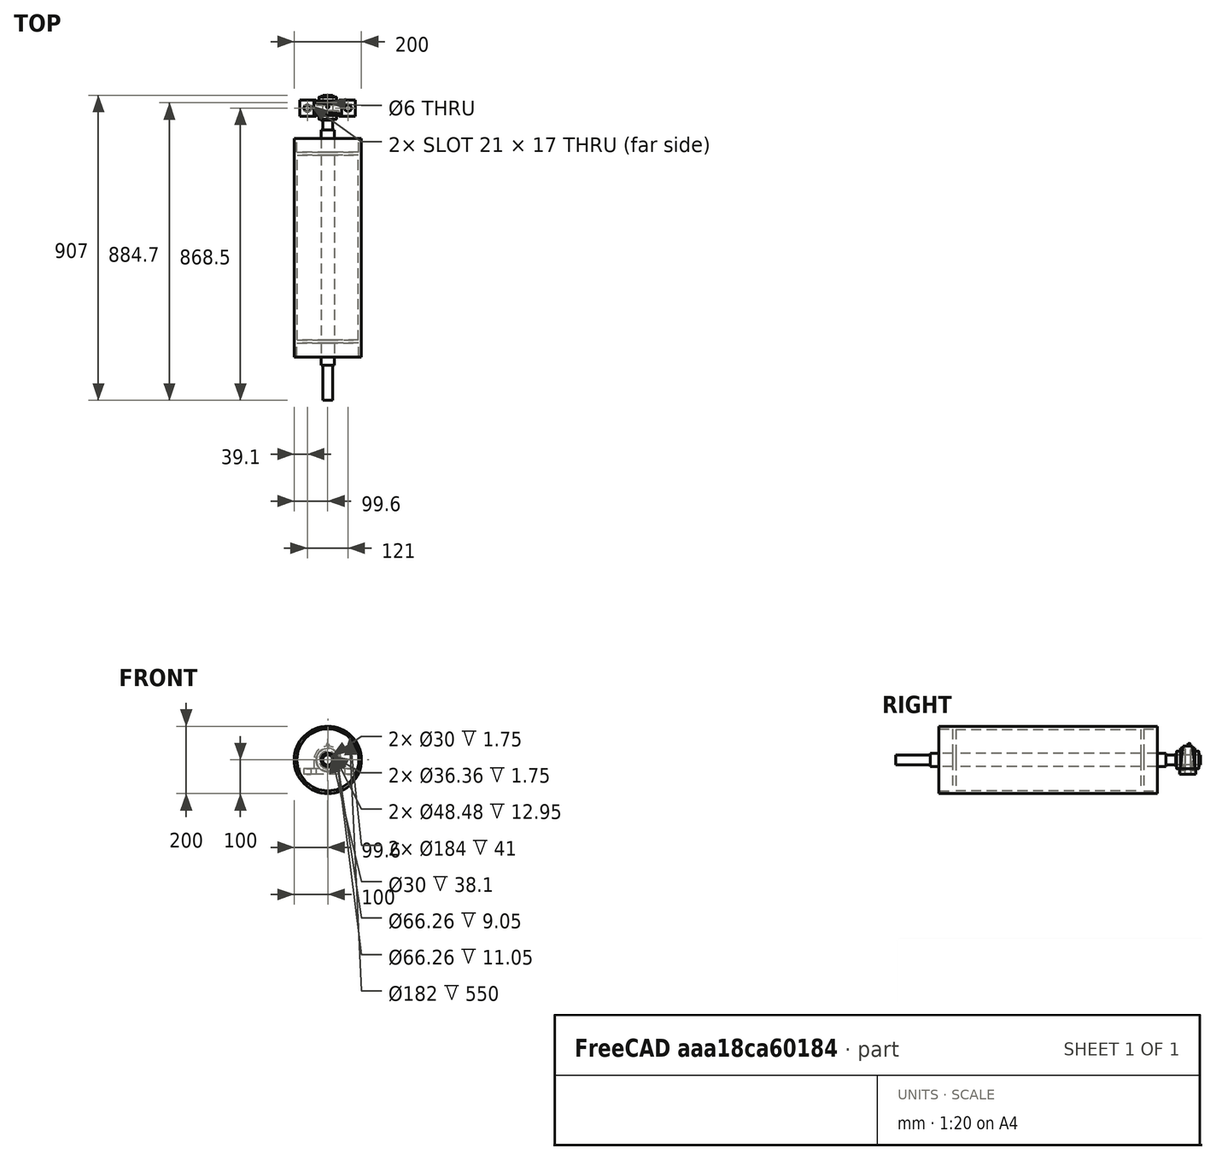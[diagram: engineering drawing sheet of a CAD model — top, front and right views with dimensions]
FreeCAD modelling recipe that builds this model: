
FCSTD DOCUMENT  (FreeCAD 0.21R33668 +26 (Git))
Label: BendPulley
License: All rights reserved
LicenseURL: https://en.wikipedia.org/wiki/All_rights_reserved
objects: Part::FeaturePython×2, Part::Feature×1, App::Part×1
note: 3 computed .brp shape members not serialized (recipe doc carries the construction recipe); baked Part::Feature solids carry a one-line shape summary decoded from their .brp

FEATURE [Part::FeaturePython] BendPulley  label="bendPulley"  # WARN: FeaturePython — macro-defined, semantics opaque (R4)
  A = 50
  B = 103.5
  C = 700
  D = 200
  E = 0
  L = 650
  Placement = pos=(0,0,0) rot=(0,0,1;4.71239rad)
  d1 = 40
  d2 = 30
  d3 = 0
  t1 = 9
  t2 = 9
  t3 = 8
  t4 = 8
FEATURE [Part::Feature] Part__Feature  label="UCP206FC"
  Placement = pos=(-0.4,-415,1.067e-13) rot=(1,0,0;1.5708rad)
  shape: bbox 165 x 70 x 92.1 mm, 127 faces (baked)
FEATURE [Part::FeaturePython] Clone  label="UCP206FC001"  # Draft clone (typed FeaturePython)
  AttacherType = Attacher::AttachEngine3D
  Fuse = false
  Objects = -> [Part__Feature]
  Placement = pos=(-0.4,415,1.067e-13) rot=(0,0.707107,0.707107;3.14159rad)
  Scale = (1,1,1)
FEATURE [App::Part] Part  label="BendPulley"
  Group = -> [Clone,Part__Feature,BendPulley]
  Origin = -> Origin
